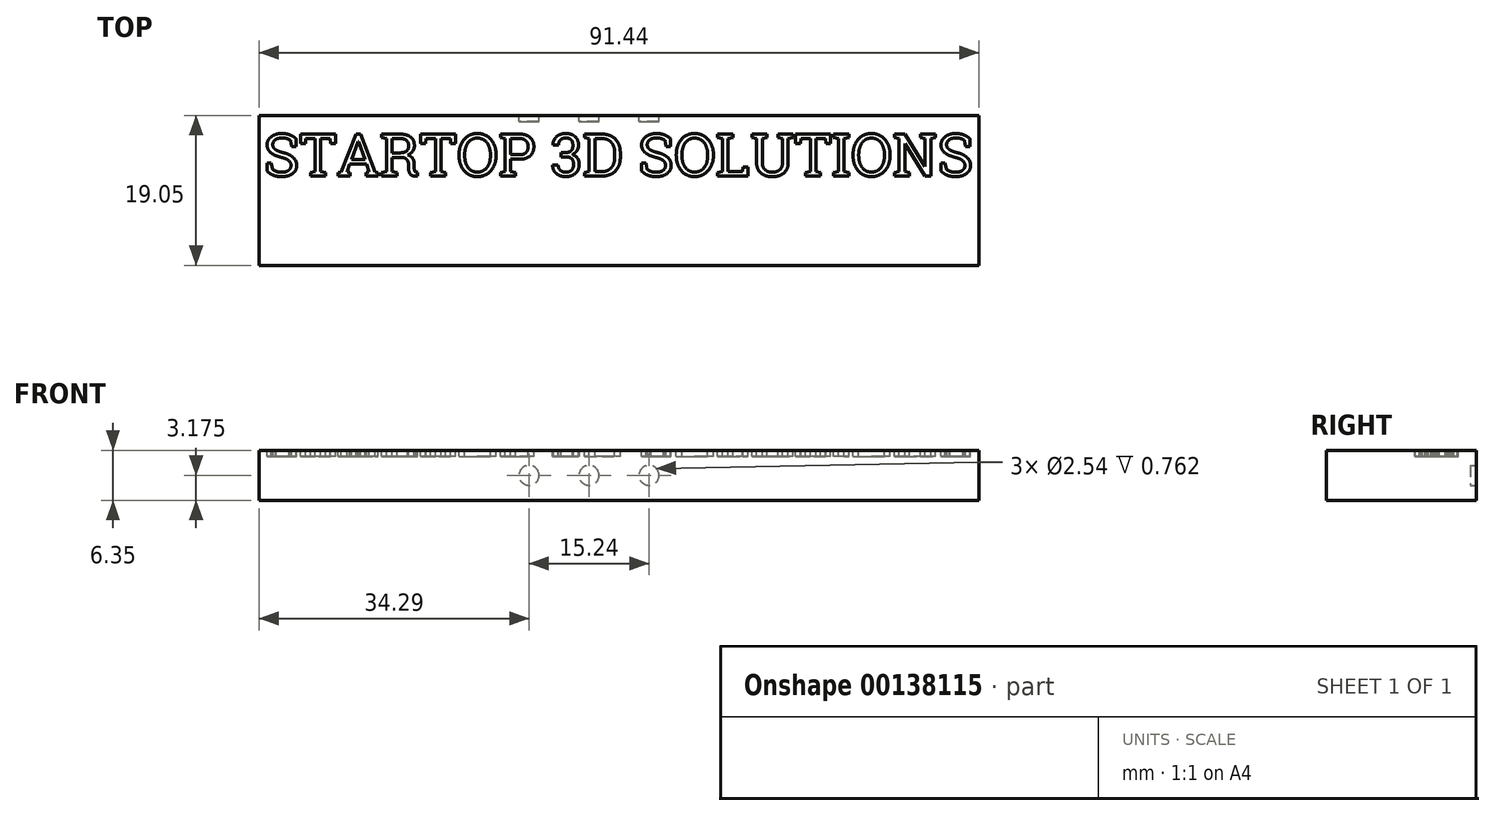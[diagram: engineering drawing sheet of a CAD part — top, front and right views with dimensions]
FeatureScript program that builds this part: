
annotation { "Feature Type Name" : "Feature", "Feature Type Description" : "" }
export const myFeature = defineFeature(function(context is Context, id is Id, definition is map)
    precondition{}
    {
        {
            var Q0;
            Q0=qCreatedBy(makeId("Top.planeOp"),FACE);
            var sketch = newSketch(context, id + "F0", { "sketchPlane" : qUnion([Q0])});
            skLineSegment(sketch, "E0.bottom", {"start": v(0, 0) * mm, "end": v(91.44, 0) * mm});
            skLineSegment(sketch, "E0.top", {"start": v(0, 19.05) * mm, "end": v(91.44, 19.05) * mm});
            skLineSegment(sketch, "E0.left", {"start": v(0, 0) * mm, "end": v(0, 19.05) * mm});
            skLineSegment(sketch, "E0.right", {"start": v(91.44, 0) * mm, "end": v(91.44, 19.05) * mm});
            skSolve(sketch);
        }
        {
            var Q0;
            Q0=qSketchRegion(id+"F0",true);
            extrude(context, id + "F1", {"entities" : qUnion([Q0]), "depth" : 6.35 * mm});
        }
        {
            var Q0;
            Q0=makeQuery(id+"F1.opExtrude","CAP_FACE",FACE,{"disambiguationData":[OSD([sQuery(id+"F0.wireOp",EDGE,"E0.bottom"),sQuery(id+"F0.wireOp",EDGE,"E0.top"),sQuery(id+"F0.wireOp",EDGE,"E0.left"),sQuery(id+"F0.wireOp",EDGE,"E0.right")])],"isStart":false});
            var sketch = newSketch(context, id + "F2", { "sketchPlane" : qUnion([Q0])});
            skLineSegment(sketch, "E1", {"start": v(0, 9.53) * mm, "end": v(91.44, 9.53) * mm, "construction": true});
            skText(sketch, "E2", { "text": "STARTOP 3D SOLUTIONS", "fontName": "RobotoSlab-Regular.ttf"});
            const initialGuessF2  = {"E2": [0.00056, 0.01135, 1, 0, 0.0054]};
            skSetInitialGuess(sketch, initialGuessF2);
            skSolve(sketch);
        }
        {
            var Q0;
            Q0=qSketchRegion(id+"F2",true);
            extrude(context, id + "F3", {"entities" : qUnion([Q0]), "operationType" : NewBodyOperationType.REMOVE, "oppositeDirection" : true, "depth" : 0.76 * mm});
        }
        {
            var Q0;
            Q0=makeQuery(id+"F1.opExtrude","SWEPT_FACE",FACE,{"disambiguationData":[OSD([sQuery(id+"F0.wireOp",EDGE,"E0.top")])]});
            var sketch = newSketch(context, id + "F4", { "sketchPlane" : qUnion([Q0])});
            skLineSegment(sketch, "E3", {"start": v(-91.44, 3.18) * mm, "end": v(0, 3.18) * mm, "construction": true});
            skCircle(sketch, "E4", {"center": v(-49.53, 3.17) * mm, "radius": 1.27 * mm});
            skLineSegment(sketch, "E5.MirrorCS", {"start": v(0, 3.18) * mm, "end": v(-91.44, 3.17) * mm, "construction": true});
            skCircle(sketch, "E6.MirrorC", {"center": v(-41.91, 3.17) * mm, "radius": 1.27 * mm});
            skCircle(sketch, "E7.MirrorC", {"center": v(-34.3, 3.17) * mm, "radius": 1.27 * mm});
            skSolve(sketch);
        }
        {
            var Q0;
            Q0 = qSketchRegion(id + "F4", true);
            extrude(context, id + "F5", {"entities" : qUnion([Q0]), "operationType" : NewBodyOperationType.REMOVE, "oppositeDirection" : true, "depth" : 0.76 * mm});
        }
    });
